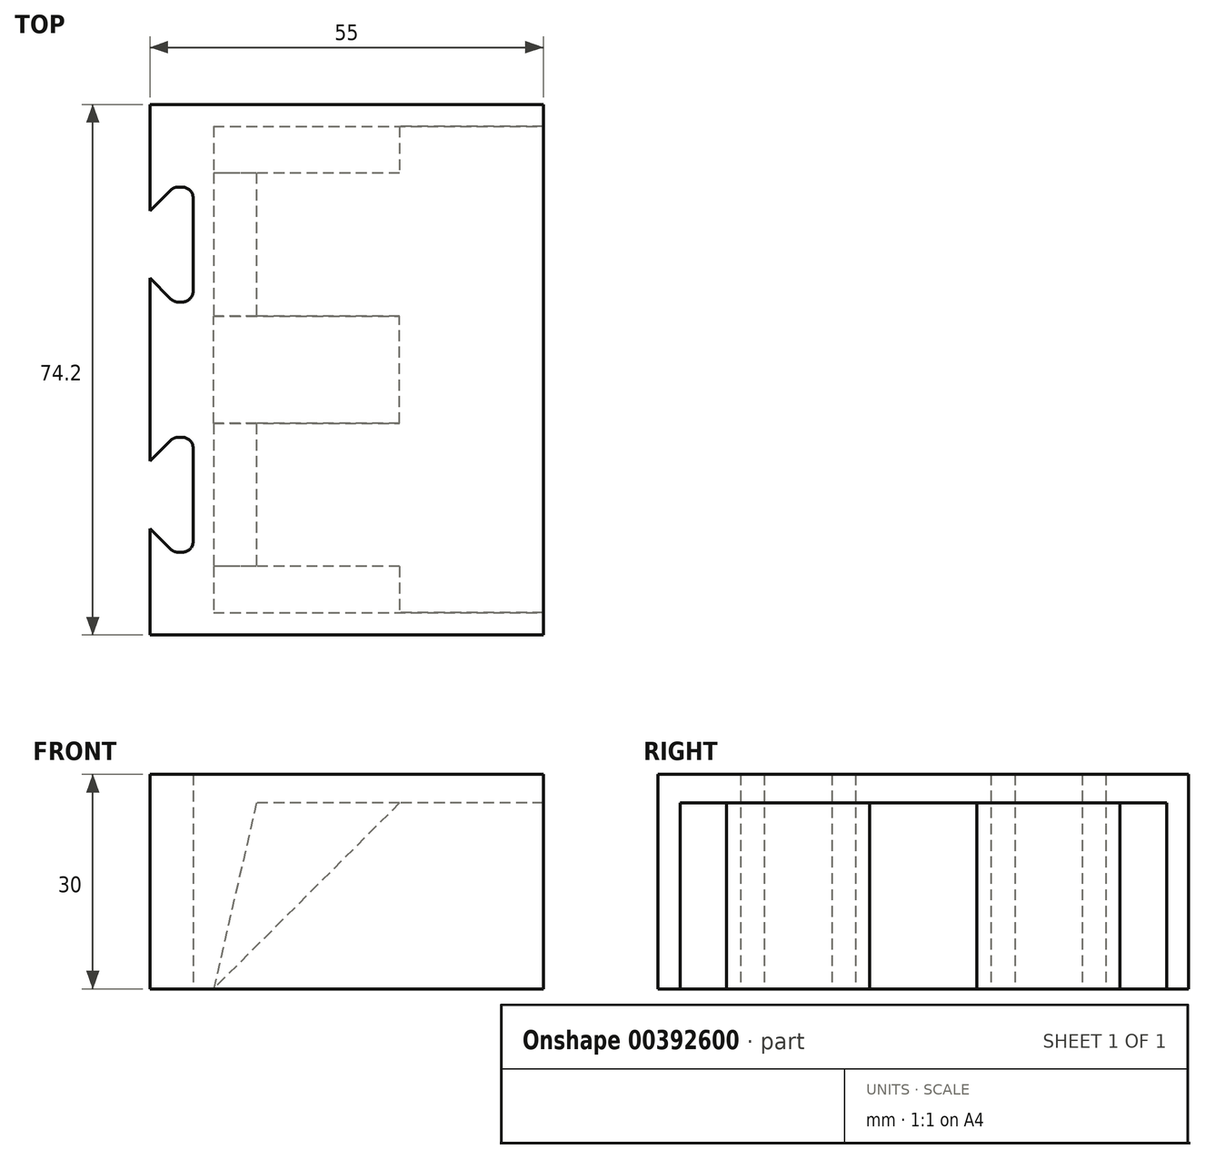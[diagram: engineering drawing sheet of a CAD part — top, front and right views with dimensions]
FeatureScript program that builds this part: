
annotation { "Feature Type Name" : "Feature", "Feature Type Description" : "" }
export const myFeature = defineFeature(function(context is Context, id is Id, definition is map)
    precondition{}
    {
        {
            var Q0;
            Q0=qCreatedBy(makeId("Top.planeOp"),FACE);
            var sketch = newSketch(context, id + "F0", { "sketchPlane" : qUnion([Q0])});
            skLineSegment(sketch, "E0.bottom", {"start": v(90, -35) * mm, "end": v(0, -35) * mm});
            skLineSegment(sketch, "E0.top", {"start": v(90, 35) * mm, "end": v(0, 35) * mm});
            skLineSegment(sketch, "E0.left", {"start": v(90, -35) * mm, "end": v(90, 35) * mm});
            skPoint(sketch, "E0.middle", {"position": v(0, 0) * mm});
            skPoint(sketch, "E1.middle", {"position": v(49.8, 0) * mm});
            skLineSegment(sketch, "E2", {"start": v(0, 0) * mm, "end": v(24, 0) * mm, "construction": true});
            skLineSegment(sketch, "E3", {"start": v(0, 0) * mm, "end": v(0, -14) * mm, "construction": true});
            skLineSegment(sketch, "E4", {"start": v(0, 0) * mm, "end": v(-35, 0) * mm, "construction": true});
            skLineSegment(sketch, "E5.bottom", {"start": v(-5, -19.5) * mm, "end": v(5, -19.5) * mm});
            skLineSegment(sketch, "E5.top", {"start": v(-5, 19.5) * mm, "end": v(5, 19.5) * mm});
            skLineSegment(sketch, "E5.left", {"start": v(-5, -19.5) * mm, "end": v(-5, 19.5) * mm});
            skLineSegment(sketch, "E5.right", {"start": v(5, -19.5) * mm, "end": v(5, 19.5) * mm});
            skLineSegment(sketch, "E6.bottom", {"start": v(-40, -17.25) * mm, "end": v(-30, -17.25) * mm});
            skLineSegment(sketch, "E6.top", {"start": v(-40, 17.25) * mm, "end": v(-30, 17.25) * mm});
            skLineSegment(sketch, "E6.left", {"start": v(-40, -17.25) * mm, "end": v(-40, 17.25) * mm});
            skLineSegment(sketch, "E6.right", {"start": v(-30, -17.25) * mm, "end": v(-30, 17.25) * mm});
            skPoint(sketch, "E6.middle", {"position": v(-35, 0) * mm});
            skLineSegment(sketch, "E7", {"start": v(0, 35) * mm, "end": v(0, 23) * mm});
            skPoint(sketch, "E7.endSnap0", {"position": v(0, 35) * mm});
            skLineSegment(sketch, "E8", {"start": v(0, 23) * mm, "end": v(-50, 23) * mm});
            skLineSegment(sketch, "E9", {"start": v(-50, 23) * mm, "end": v(-50, 0) * mm});
            skLineSegment(sketch, "E10.MirrorCS", {"start": v(-50, -23) * mm, "end": v(-50, 0) * mm});
            skLineSegment(sketch, "E11.MirrorCS", {"start": v(0, -35) * mm, "end": v(0, -23) * mm});
            skLineSegment(sketch, "E12.MirrorCS", {"start": v(0, -23) * mm, "end": v(-50, -23) * mm});
            skPoint(sketch, "E0.right.end.orphan", {"position": v(-90, 35) * mm});
            skPoint(sketch, "E13.orphan", {"position": v(-90, -35) * mm});
            skLineSegment(sketch, "E14.0", {"start": v(92.1, -37.1) * mm, "end": v(92.1, 37.1) * mm});
            skLineSegment(sketch, "E14.1", {"start": v(92.1, -37.1) * mm, "end": v(-2.1, -37.1) * mm});
            skLineSegment(sketch, "E14.2", {"start": v(92.1, 37.1) * mm, "end": v(-2.1, 37.1) * mm});
            skLineSegment(sketch, "E14.3", {"start": v(-2.1, -37.1) * mm, "end": v(-2.1, -25.1) * mm});
            skLineSegment(sketch, "E14.4", {"start": v(-2.1, -25.1) * mm, "end": v(-52.1, -25.1) * mm});
            skLineSegment(sketch, "E14.5", {"start": v(-2.1, 37.1) * mm, "end": v(-2.1, 25.1) * mm});
            skLineSegment(sketch, "E14.6", {"start": v(-2.1, 25.1) * mm, "end": v(-52.1, 25.1) * mm});
            skLineSegment(sketch, "E14.7", {"start": v(-52.1, 25.1) * mm, "end": v(-52.1, 0) * mm});
            skLineSegment(sketch, "E14.8", {"start": v(-52.1, -25.1) * mm, "end": v(-52.1, 0) * mm});
            skLineSegment(sketch, "E15.bottom", {"start": v(-30, 52.75) * mm, "end": v(-40, 52.75) * mm});
            skLineSegment(sketch, "E15.top", {"start": v(-30, 87.25) * mm, "end": v(-40, 87.25) * mm});
            skLineSegment(sketch, "E15.left", {"start": v(-30, 52.75) * mm, "end": v(-30, 87.25) * mm});
            skLineSegment(sketch, "E15.right", {"start": v(-40, 52.75) * mm, "end": v(-40, 87.25) * mm});
            skPoint(sketch, "E15.middle", {"position": v(-35, 70) * mm});
            skLineSegment(sketch, "E16.bottom", {"start": v(-5, 50.5) * mm, "end": v(5, 50.5) * mm});
            skLineSegment(sketch, "E16.top", {"start": v(-5, 89.5) * mm, "end": v(5, 89.5) * mm});
            skLineSegment(sketch, "E16.left", {"start": v(-5, 50.5) * mm, "end": v(-5, 89.5) * mm});
            skLineSegment(sketch, "E16.right", {"start": v(5, 50.5) * mm, "end": v(5, 89.5) * mm});
            skPoint(sketch, "E16.middle", {"position": v(0, 70) * mm});
            skPoint(sketch, "E16.middle.positionSnap0", {"position": v(-30, 70) * mm});
            skPoint(sketch, "E16.centerSnap0", {"position": v(-30, 70) * mm});
            skLineSegment(sketch, "E17", {"start": v(-35, 0) * mm, "end": v(-35, 70) * mm, "construction": true});
            skCircle(sketch, "E18", {"center": v(0, -14) * mm, "radius": 2 * mm});
            skLineSegment(sketch, "E19", {"start": v(-35, 0) * mm, "end": v(-35, -11.75) * mm, "construction": true});
            skCircle(sketch, "E20", {"center": v(-35, -11.75) * mm, "radius": 2 * mm});
            skCircle(sketch, "E21.MirrorC", {"center": v(-35, 11.75) * mm, "radius": 2 * mm});
            skCircle(sketch, "E22.MirrorC", {"center": v(0, 14) * mm, "radius": 2 * mm});
            skLineSegment(sketch, "E23", {"start": v(-35, 70) * mm, "end": v(-35, 81.75) * mm, "construction": true});
            skLineSegment(sketch, "E24", {"start": v(0, 70) * mm, "end": v(0, 84) * mm, "construction": true});
            skCircle(sketch, "E25", {"center": v(-35, 81.75) * mm, "radius": 2 * mm});
            skCircle(sketch, "E26", {"center": v(0, 84) * mm, "radius": 2 * mm});
            skLineSegment(sketch, "E27", {"start": v(-35, 70) * mm, "end": v(-30, 70) * mm, "construction": true});
            skCircle(sketch, "E28.MirrorC", {"center": v(-35, 58.25) * mm, "radius": 2 * mm});
            skCircle(sketch, "E29.MirrorC", {"center": v(0, 56) * mm, "radius": 2 * mm});
            skLineSegment(sketch, "E30", {"start": v(90, -35) * mm, "end": v(92.1, -35) * mm});
            skLineSegment(sketch, "E31", {"start": v(90, 35) * mm, "end": v(92.1, 35) * mm});
            skLineSegment(sketch, "E32", {"start": v(-2.1, 37.1) * mm, "end": v(-6.1, 37.1) * mm});
            skLineSegment(sketch, "E33", {"start": v(-6.1, 37.1) * mm, "end": v(-6.1, 25.1) * mm});
            skLineSegment(sketch, "E34", {"start": v(-2.1, -37.1) * mm, "end": v(-6.1, -37.1) * mm});
            skLineSegment(sketch, "E35", {"start": v(-6.1, -37.1) * mm, "end": v(-6.1, -25.1) * mm});
            skLineSegment(sketch, "E36", {"start": v(-41, 23) * mm, "end": v(-41, 11) * mm});
            skLineSegment(sketch, "E37", {"start": v(-41, 11) * mm, "end": v(-50, 11) * mm});
            skPoint(sketch, "E38.end.orphan", {"position": v(-41, 14.45) * mm});
            skLineSegment(sketch, "E39.MirrorCS", {"start": v(-41, -11) * mm, "end": v(-50, -11) * mm});
            skLineSegment(sketch, "E40.MirrorCS", {"start": v(-41, -23) * mm, "end": v(-41, -11) * mm});
            skLineSegment(sketch, "E41", {"start": v(90, -35) * mm, "end": v(90, -37.1) * mm});
            skLineSegment(sketch, "E42", {"start": v(90, 35) * mm, "end": v(90, 37.1) * mm});
            skLineSegment(sketch, "E43.bottom", {"start": v(90, 35) * mm, "end": v(86, 35) * mm});
            skLineSegment(sketch, "E43.left", {"start": v(90, 35) * mm, "end": v(90, 23) * mm});
            skLineSegment(sketch, "E44.bottom", {"start": v(90, -35) * mm, "end": v(86, -35) * mm});
            skLineSegment(sketch, "E44.left", {"start": v(90, -35) * mm, "end": v(90, -23) * mm});
            skLineSegment(sketch, "E45.bottom", {"start": v(86, -35) * mm, "end": v(80, -35) * mm});
            skLineSegment(sketch, "E46.bottom", {"start": v(86, 35) * mm, "end": v(80, 35) * mm});
            skLineSegment(sketch, "E47.bottom", {"start": v(0, 23) * mm, "end": v(7, 23) * mm});
            skLineSegment(sketch, "E47.top", {"start": v(0, 35) * mm, "end": v(12, 35) * mm});
            skLineSegment(sketch, "E47.left", {"start": v(0, 23) * mm, "end": v(0, 35) * mm});
            skLineSegment(sketch, "E47.right", {"start": v(12, 28) * mm, "end": v(12, 35) * mm});
            skLineSegment(sketch, "E48.bottom", {"start": v(0, -35) * mm, "end": v(12, -35) * mm});
            skLineSegment(sketch, "E48.top", {"start": v(0, -23) * mm, "end": v(7, -23) * mm});
            skLineSegment(sketch, "E48.right", {"start": v(12, -35) * mm, "end": v(12, -28) * mm});
            skCircle(sketch, "E49", {"center": v(6, -29) * mm, "radius": 2 * mm});
            skPoint(sketch, "E49.centerSnap0", {"position": v(6, -35) * mm});
            skPoint(sketch, "E49.centerSnap1", {"position": v(0, -29) * mm});
            skPoint(sketch, "E50.visualSharp", {"position": v(12, -23) * mm});
            skArc(sketch, "E50.filletArc", {"start": v(12, -28) * mm, "mid": v(10.54, -24.46) * mm, "end": v(7, -23) * mm});
            skPoint(sketch, "E51.visualSharp", {"position": v(12, 23) * mm});
            skArc(sketch, "E51.filletArc", {"start": v(7, 23) * mm, "mid": v(10.54, 24.46) * mm, "end": v(12, 28) * mm});
            skCircle(sketch, "E52.MirrorC", {"center": v(6, 29) * mm, "radius": 2 * mm});
            skCircle(sketch, "E53", {"center": v(6, 29) * mm, "radius": 4.5 * mm});
            skCircle(sketch, "E54.MirrorC", {"center": v(6, -29) * mm, "radius": 4.5 * mm});
            skCircle(sketch, "E55", {"center": v(0, 14) * mm, "radius": 6 * mm});
            skCircle(sketch, "E56", {"center": v(-35, 11.75) * mm, "radius": 6 * mm});
            skCircle(sketch, "E57", {"center": v(-35, -11.75) * mm, "radius": 6 * mm});
            skCircle(sketch, "E58", {"center": v(0, -14) * mm, "radius": 6 * mm});
            skLineSegment(sketch, "E59", {"start": v(-6.1, 25.1) * mm, "end": v(-6.08, 23) * mm});
            skLineSegment(sketch, "E60", {"start": v(-6.1, -25.1) * mm, "end": v(-6.1, -23) * mm});
            skLineSegment(sketch, "E61", {"start": v(-47.66, 23) * mm, "end": v(-47.66, 18) * mm, "construction": true});
            skLineSegment(sketch, "E62", {"start": v(-50, 18) * mm, "end": v(-45, 18) * mm, "construction": true});
            skCircle(sketch, "E63", {"center": v(-45, 18) * mm, "radius": 2.25 * mm});
            skCircle(sketch, "E64.MirrorC", {"center": v(-45, -18) * mm, "radius": 2.25 * mm});
            skCircle(sketch, "E65.MirrorC", {"center": v(-25, 18) * mm, "radius": 2.25 * mm});
            skCircle(sketch, "E66.MirrorC", {"center": v(-25, -18) * mm, "radius": 2.25 * mm});
            skCircle(sketch, "E67.MirrorC", {"center": v(28.54, -17.75) * mm, "radius": 2.25 * mm});
            skLineSegment(sketch, "E68.bottom", {"start": v(34.04, -22.75) * mm, "end": v(23.04, -22.75) * mm});
            skLineSegment(sketch, "E68.top", {"start": v(34.04, -12.75) * mm, "end": v(23.04, -12.75) * mm});
            skLineSegment(sketch, "E68.left", {"start": v(36.04, -20.75) * mm, "end": v(36.04, -14.75) * mm});
            skLineSegment(sketch, "E68.right", {"start": v(21.04, -20.75) * mm, "end": v(21.04, -14.75) * mm});
            skLineSegment(sketch, "E69.0", {"start": v(36.44, -12.35) * mm, "end": v(20.64, -12.35) * mm});
            skLineSegment(sketch, "E69.1", {"start": v(36.44, -23.15) * mm, "end": v(36.44, -12.35) * mm});
            skLineSegment(sketch, "E69.2", {"start": v(36.44, -23.15) * mm, "end": v(20.64, -23.15) * mm});
            skLineSegment(sketch, "E69.3", {"start": v(20.64, -23.15) * mm, "end": v(20.64, -12.35) * mm});
            skPoint(sketch, "E70.visualSharp", {"position": v(21.04, -12.75) * mm});
            skArc(sketch, "E70.filletArc", {"start": v(23.04, -12.75) * mm, "mid": v(21.62, -13.33) * mm, "end": v(21.04, -14.75) * mm});
            skPoint(sketch, "E71.visualSharp", {"position": v(36.04, -12.75) * mm});
            skArc(sketch, "E71.filletArc", {"start": v(36.04, -14.75) * mm, "mid": v(35.45, -13.33) * mm, "end": v(34.04, -12.75) * mm});
            skPoint(sketch, "E72.visualSharp", {"position": v(36.04, -22.75) * mm});
            skArc(sketch, "E72.filletArc", {"start": v(34.04, -22.75) * mm, "mid": v(35.45, -22.16) * mm, "end": v(36.04, -20.75) * mm});
            skPoint(sketch, "E73.visualSharp", {"position": v(21.04, -22.75) * mm});
            skArc(sketch, "E73.filletArc", {"start": v(21.04, -20.75) * mm, "mid": v(21.62, -22.16) * mm, "end": v(23.04, -22.75) * mm});
            skArc(sketch, "E74.0", {"start": v(39.54, -14.75) * mm, "mid": v(37.93, -10.86) * mm, "end": v(34.04, -9.25) * mm});
            skLineSegment(sketch, "E74.1", {"start": v(39.54, -20.75) * mm, "end": v(39.54, -14.75) * mm});
            skLineSegment(sketch, "E74.2", {"start": v(34.04, -9.25) * mm, "end": v(23.04, -9.25) * mm});
            skArc(sketch, "E74.3", {"start": v(34.04, -26.25) * mm, "mid": v(37.93, -24.64) * mm, "end": v(39.54, -20.75) * mm});
            skArc(sketch, "E74.4", {"start": v(23.04, -9.25) * mm, "mid": v(19.15, -10.86) * mm, "end": v(17.54, -14.75) * mm});
            skLineSegment(sketch, "E74.5", {"start": v(17.54, -20.75) * mm, "end": v(17.54, -14.75) * mm});
            skArc(sketch, "E74.6", {"start": v(17.54, -20.75) * mm, "mid": v(19.15, -24.64) * mm, "end": v(23.04, -26.25) * mm});
            skLineSegment(sketch, "E74.7", {"start": v(34.04, -26.25) * mm, "end": v(23.04, -26.25) * mm});
            skLineSegment(sketch, "E75", {"start": v(45, 37.1) * mm, "end": v(45, -37.1) * mm});
            skLineSegment(sketch, "E76", {"start": v(45, 31.57) * mm, "end": v(68, 31.57) * mm, "construction": true});
            skLineSegment(sketch, "E77", {"start": v(68, 35) * mm, "end": v(68, -35) * mm});
            skLineSegment(sketch, "E78", {"start": v(12, -28) * mm, "end": v(12, 28) * mm});
            skLineSegment(sketch, "E79", {"start": v(12, 35) * mm, "end": v(12, 37.1) * mm});
            skLineSegment(sketch, "E80", {"start": v(68, 35) * mm, "end": v(68, 37.1) * mm});
            skLineSegment(sketch, "E81", {"start": v(68, 31.57) * mm, "end": v(70.1, 31.57) * mm, "construction": true});
            skLineSegment(sketch, "E82", {"start": v(70.1, 37.1) * mm, "end": v(70.1, -37.1) * mm});
            skLineSegment(sketch, "E83", {"start": v(12, -35) * mm, "end": v(12, -37.1) * mm});
            skLineSegment(sketch, "E84", {"start": v(72.96, 0) * mm, "end": v(72.96, 17.5) * mm, "construction": true});
            skPoint(sketch, "E84.startSnap0", {"position": v(70.1, 0) * mm});
            skLineSegment(sketch, "E85", {"start": v(70.1, 13.5) * mm, "end": v(73.34, 10.26) * mm});
            skPoint(sketch, "E86.end.orphan", {"position": v(71.21, 13.5) * mm});
            skPoint(sketch, "E86.start.orphan", {"position": v(71.21, 17.5) * mm});
            skLineSegment(sketch, "E87", {"start": v(74.05, 9.96) * mm, "end": v(74.64, 9.96) * mm});
            skLineSegment(sketch, "E88", {"start": v(72.96, 17.5) * mm, "end": v(71.21, 17.5) * mm, "construction": true});
            skLineSegment(sketch, "E89.MirrorCS", {"start": v(70.1, 21.5) * mm, "end": v(73.34, 24.74) * mm});
            skLineSegment(sketch, "E90.MirrorCS", {"start": v(74.05, 25.04) * mm, "end": v(74.64, 25.04) * mm});
            skLineSegment(sketch, "E91", {"start": v(75.64, 24.04) * mm, "end": v(75.64, 10.96) * mm});
            skPoint(sketch, "E92.visualSharp", {"position": v(75.64, 25.04) * mm});
            skArc(sketch, "E92.filletArc", {"start": v(75.64, 24.04) * mm, "mid": v(75.34, 24.74) * mm, "end": v(74.64, 25.04) * mm});
            skPoint(sketch, "E93.visualSharp", {"position": v(73.64, 25.04) * mm});
            skArc(sketch, "E93.filletArc", {"start": v(74.05, 25.04) * mm, "mid": v(73.67, 24.96) * mm, "end": v(73.34, 24.74) * mm});
            skPoint(sketch, "E94.visualSharp", {"position": v(73.64, 9.96) * mm});
            skArc(sketch, "E94.filletArc", {"start": v(73.34, 10.26) * mm, "mid": v(73.67, 10.04) * mm, "end": v(74.05, 9.96) * mm});
            skPoint(sketch, "E95.visualSharp", {"position": v(75.64, 9.96) * mm});
            skArc(sketch, "E95.filletArc", {"start": v(74.64, 9.96) * mm, "mid": v(75.34, 10.26) * mm, "end": v(75.64, 10.96) * mm});
            skLineSegment(sketch, "E96.MirrorCS", {"start": v(70.1, -13.5) * mm, "end": v(73.34, -10.26) * mm});
            skArc(sketch, "E97.MirrorCS", {"start": v(73.34, -10.26) * mm, "mid": v(73.67, -10.04) * mm, "end": v(74.05, -9.96) * mm});
            skLineSegment(sketch, "E98.MirrorCS", {"start": v(74.05, -9.96) * mm, "end": v(74.64, -9.96) * mm});
            skArc(sketch, "E99.MirrorCS", {"start": v(74.64, -9.96) * mm, "mid": v(75.34, -10.26) * mm, "end": v(75.64, -10.96) * mm});
            skLineSegment(sketch, "E100.MirrorCS", {"start": v(75.64, -24.04) * mm, "end": v(75.64, -10.96) * mm});
            skLineSegment(sketch, "E101.MirrorCS", {"start": v(70.1, -21.5) * mm, "end": v(73.34, -24.74) * mm});
            skArc(sketch, "E102.MirrorCS", {"start": v(74.05, -25.04) * mm, "mid": v(73.67, -24.96) * mm, "end": v(73.34, -24.74) * mm});
            skLineSegment(sketch, "E103.MirrorCS", {"start": v(74.05, -25.04) * mm, "end": v(74.64, -25.04) * mm});
            skArc(sketch, "E104.MirrorCS", {"start": v(75.64, -24.04) * mm, "mid": v(75.34, -24.74) * mm, "end": v(74.64, -25.04) * mm});
            skLineSegment(sketch, "E105", {"start": v(68, -35) * mm, "end": v(56.64, -23.64) * mm, "construction": true});
            skArc(sketch, "E106.MirrorCS", {"start": v(43.26, -40.34) * mm, "mid": v(43.04, -40.67) * mm, "end": v(42.96, -41.05) * mm});
            skArc(sketch, "E107.MirrorCS", {"start": v(58.04, -41.05) * mm, "mid": v(57.96, -40.67) * mm, "end": v(57.74, -40.34) * mm});
            skArc(sketch, "E108.MirrorCS", {"start": v(42.96, -41.64) * mm, "mid": v(43.26, -42.34) * mm, "end": v(43.96, -42.64) * mm});
            skArc(sketch, "E109.MirrorCS", {"start": v(57.04, -42.64) * mm, "mid": v(57.74, -42.34) * mm, "end": v(58.04, -41.64) * mm});
            skLineSegment(sketch, "E110.MirrorCS", {"start": v(42.96, -41.05) * mm, "end": v(42.96, -41.64) * mm});
            skLineSegment(sketch, "E111.MirrorCS", {"start": v(58.04, -41.05) * mm, "end": v(58.04, -41.64) * mm});
            skLineSegment(sketch, "E112.MirrorCS", {"start": v(57.04, -42.64) * mm, "end": v(43.96, -42.64) * mm});
            skLineSegment(sketch, "E113.MirrorCS", {"start": v(46.5, -37.1) * mm, "end": v(43.26, -40.34) * mm});
            skLineSegment(sketch, "E114.MirrorCS", {"start": v(54.5, -37.1) * mm, "end": v(57.74, -40.34) * mm});
            skLineSegment(sketch, "E115", {"start": v(36.04, -37.1) * mm, "end": v(36.04, -40.15) * mm, "construction": true});
            skLineSegment(sketch, "E116.MirrorCS", {"start": v(14.04, -41.05) * mm, "end": v(14.04, -41.64) * mm});
            skArc(sketch, "E117.MirrorCS", {"start": v(14.04, -41.05) * mm, "mid": v(14.12, -40.67) * mm, "end": v(14.33, -40.34) * mm});
            skLineSegment(sketch, "E118.MirrorCS", {"start": v(29.11, -41.05) * mm, "end": v(29.11, -41.64) * mm});
            skArc(sketch, "E119.MirrorCS", {"start": v(28.82, -40.34) * mm, "mid": v(29.04, -40.67) * mm, "end": v(29.11, -41.05) * mm});
            skArc(sketch, "E120.MirrorCS", {"start": v(15.04, -42.64) * mm, "mid": v(14.33, -42.34) * mm, "end": v(14.04, -41.64) * mm});
            skLineSegment(sketch, "E121.MirrorCS", {"start": v(15.04, -42.64) * mm, "end": v(28.11, -42.64) * mm});
            skArc(sketch, "E122.MirrorCS", {"start": v(29.11, -41.64) * mm, "mid": v(28.82, -42.34) * mm, "end": v(28.11, -42.64) * mm});
            skLineSegment(sketch, "E123.MirrorCS", {"start": v(17.58, -37.1) * mm, "end": v(14.33, -40.34) * mm});
            skLineSegment(sketch, "E124.MirrorCS", {"start": v(25.58, -37.1) * mm, "end": v(28.82, -40.34) * mm});
            skLineSegment(sketch, "E125", {"start": v(28.54, -17.75) * mm, "end": v(28.54, 0) * mm, "construction": true});
            skLineSegment(sketch, "E126", {"start": v(28.54, 0) * mm, "end": v(56.04, 0) * mm, "construction": true});
            skLineSegment(sketch, "E127.bottom", {"start": v(53.54, 20) * mm, "end": v(58.54, 20) * mm});
            skLineSegment(sketch, "E127.top", {"start": v(53.54, -20) * mm, "end": v(58.54, -20) * mm});
            skLineSegment(sketch, "E127.left", {"start": v(53.54, 20) * mm, "end": v(53.54, -20) * mm});
            skLineSegment(sketch, "E127.right", {"start": v(58.54, 20) * mm, "end": v(58.54, -20) * mm});
            skPoint(sketch, "E127.middle", {"position": v(56.04, 0) * mm});
            skLineSegment(sketch, "E128", {"start": v(28.54, -17.75) * mm, "end": v(28.54, -35) * mm, "construction": true});
            skPoint(sketch, "E128.endSnap0", {"position": v(28.54, -26.25) * mm});
            skLineSegment(sketch, "E129", {"start": v(28.54, -17.75) * mm, "end": v(12, -17.75) * mm, "construction": true});
            skLineSegment(sketch, "E130", {"start": v(12, 17.54) * mm, "end": v(28.54, 17.54) * mm, "construction": true});
            skLineSegment(sketch, "E131", {"start": v(28.54, 17.54) * mm, "end": v(28.54, 35) * mm, "construction": true});
            skArc(sketch, "E132.MirrorCS", {"start": v(36.04, 14.75) * mm, "mid": v(35.45, 13.33) * mm, "end": v(34.04, 12.75) * mm});
            skArc(sketch, "E133.MirrorCS", {"start": v(23.04, 12.75) * mm, "mid": v(21.62, 13.33) * mm, "end": v(21.04, 14.75) * mm});
            skArc(sketch, "E134.MirrorCS", {"start": v(21.04, 20.75) * mm, "mid": v(21.62, 22.16) * mm, "end": v(23.04, 22.75) * mm});
            skArc(sketch, "E135.MirrorCS", {"start": v(34.04, 22.75) * mm, "mid": v(35.45, 22.16) * mm, "end": v(36.04, 20.75) * mm});
            skArc(sketch, "E136.MirrorCS", {"start": v(23.04, 9.25) * mm, "mid": v(19.15, 10.86) * mm, "end": v(17.54, 14.75) * mm});
            skLineSegment(sketch, "E137.MirrorCS", {"start": v(34.04, 9.25) * mm, "end": v(23.04, 9.25) * mm});
            skPoint(sketch, "E138.MirrorP", {"position": v(36.04, 12.75) * mm});
            skArc(sketch, "E139.MirrorCS", {"start": v(34.04, 26.25) * mm, "mid": v(37.93, 24.64) * mm, "end": v(39.54, 20.75) * mm});
            skArc(sketch, "E140.MirrorCS", {"start": v(17.54, 20.75) * mm, "mid": v(19.15, 24.64) * mm, "end": v(23.04, 26.25) * mm});
            skPoint(sketch, "E141.MirrorP", {"position": v(28.54, 17.75) * mm});
            skLineSegment(sketch, "E142.MirrorCS", {"start": v(36.44, 23.15) * mm, "end": v(20.64, 23.15) * mm});
            skPoint(sketch, "E143.MirrorP", {"position": v(21.04, 12.75) * mm});
            skLineSegment(sketch, "E144.MirrorCS", {"start": v(34.04, 26.25) * mm, "end": v(23.04, 26.25) * mm});
            skPoint(sketch, "E145.MirrorP", {"position": v(21.04, 22.75) * mm});
            skLineSegment(sketch, "E146.MirrorCS", {"start": v(20.64, 23.15) * mm, "end": v(20.64, 12.35) * mm});
            skLineSegment(sketch, "E147.MirrorCS", {"start": v(36.44, 12.35) * mm, "end": v(20.64, 12.35) * mm});
            skLineSegment(sketch, "E148.MirrorCS", {"start": v(17.54, 20.75) * mm, "end": v(17.54, 14.75) * mm});
            skCircle(sketch, "E149.MirrorC", {"center": v(28.54, 17.75) * mm, "radius": 2.25 * mm});
            skPoint(sketch, "E150.MirrorP", {"position": v(28.54, 26.25) * mm});
            skPoint(sketch, "E151.MirrorP", {"position": v(36.04, 22.75) * mm});
            skLineSegment(sketch, "E152.MirrorCS", {"start": v(21.04, 20.75) * mm, "end": v(21.04, 14.75) * mm});
            skLineSegment(sketch, "E153.MirrorCS", {"start": v(39.54, 20.75) * mm, "end": v(39.54, 14.75) * mm});
            skLineSegment(sketch, "E154.MirrorCS", {"start": v(36.44, 23.15) * mm, "end": v(36.44, 12.35) * mm});
            skLineSegment(sketch, "E155.MirrorCS", {"start": v(34.04, 22.75) * mm, "end": v(23.04, 22.75) * mm});
            skArc(sketch, "E156.MirrorCS", {"start": v(39.54, 14.75) * mm, "mid": v(37.93, 10.86) * mm, "end": v(34.04, 9.25) * mm});
            skLineSegment(sketch, "E157.MirrorCS", {"start": v(34.04, 12.75) * mm, "end": v(23.04, 12.75) * mm});
            skLineSegment(sketch, "E158.MirrorCS", {"start": v(36.04, 20.75) * mm, "end": v(36.04, 14.75) * mm});
            skArc(sketch, "E159.MirrorCS", {"start": v(29.11, 41.64) * mm, "mid": v(28.82, 42.34) * mm, "end": v(28.11, 42.64) * mm});
            skArc(sketch, "E160.MirrorCS", {"start": v(28.82, 40.34) * mm, "mid": v(29.04, 40.67) * mm, "end": v(29.11, 41.05) * mm});
            skArc(sketch, "E161.MirrorCS", {"start": v(15.04, 42.64) * mm, "mid": v(14.33, 42.34) * mm, "end": v(14.04, 41.64) * mm});
            skArc(sketch, "E162.MirrorCS", {"start": v(14.04, 41.05) * mm, "mid": v(14.12, 40.67) * mm, "end": v(14.33, 40.34) * mm});
            skArc(sketch, "E163.MirrorCS", {"start": v(57.04, 42.64) * mm, "mid": v(57.74, 42.34) * mm, "end": v(58.04, 41.64) * mm});
            skArc(sketch, "E164.MirrorCS", {"start": v(58.04, 41.05) * mm, "mid": v(57.96, 40.67) * mm, "end": v(57.74, 40.34) * mm});
            skLineSegment(sketch, "E165.MirrorCS", {"start": v(42.96, 41.05) * mm, "end": v(42.96, 41.64) * mm});
            skLineSegment(sketch, "E166.MirrorCS", {"start": v(58.04, 41.05) * mm, "end": v(58.04, 41.64) * mm});
            skLineSegment(sketch, "E167.MirrorCS", {"start": v(14.04, 41.05) * mm, "end": v(14.04, 41.64) * mm});
            skLineSegment(sketch, "E168.MirrorCS", {"start": v(29.11, 41.05) * mm, "end": v(29.11, 41.64) * mm});
            skArc(sketch, "E169.MirrorCS", {"start": v(42.96, 41.64) * mm, "mid": v(43.26, 42.34) * mm, "end": v(43.96, 42.64) * mm});
            skArc(sketch, "E170.MirrorCS", {"start": v(43.26, 40.34) * mm, "mid": v(43.04, 40.67) * mm, "end": v(42.96, 41.05) * mm});
            skLineSegment(sketch, "E171.MirrorCS", {"start": v(57.04, 42.64) * mm, "end": v(43.96, 42.64) * mm});
            skLineSegment(sketch, "E172.MirrorCS", {"start": v(15.04, 42.64) * mm, "end": v(28.11, 42.64) * mm});
            skLineSegment(sketch, "E173.MirrorCS", {"start": v(17.58, 37.1) * mm, "end": v(14.33, 40.34) * mm});
            skLineSegment(sketch, "E174.MirrorCS", {"start": v(25.58, 37.1) * mm, "end": v(28.82, 40.34) * mm});
            skLineSegment(sketch, "E175.MirrorCS", {"start": v(46.5, 37.1) * mm, "end": v(43.26, 40.34) * mm});
            skLineSegment(sketch, "E176.MirrorCS", {"start": v(54.5, 37.1) * mm, "end": v(57.74, 40.34) * mm});
            skLineSegment(sketch, "E177", {"start": v(92.1, 37.1) * mm, "end": v(125.1, 37.1) * mm});
            skLineSegment(sketch, "E178", {"start": v(125.1, 37.1) * mm, "end": v(125.1, -37.1) * mm});
            skLineSegment(sketch, "E179", {"start": v(125.1, -37.1) * mm, "end": v(92.1, -37.1) * mm});
            skLineSegment(sketch, "E180", {"start": v(125.1, 30.14) * mm, "end": v(123, 30.14) * mm, "construction": true});
            skLineSegment(sketch, "E181.0", {"start": v(70.1, 12.8) * mm, "end": v(72.99, 9.9) * mm});
            skArc(sketch, "E181.1", {"start": v(72.99, 9.9) * mm, "mid": v(73.48, 9.58) * mm, "end": v(74.05, 9.46) * mm});
            skLineSegment(sketch, "E181.2", {"start": v(74.05, 9.46) * mm, "end": v(74.64, 9.46) * mm});
            skArc(sketch, "E181.3", {"start": v(74.64, 9.46) * mm, "mid": v(75.7, 9.9) * mm, "end": v(76.14, 10.96) * mm});
            skLineSegment(sketch, "E181.4", {"start": v(76.14, 24.04) * mm, "end": v(76.14, 10.96) * mm});
            skLineSegment(sketch, "E181.5", {"start": v(70.1, 22.2) * mm, "end": v(72.99, 25.1) * mm});
            skArc(sketch, "E181.6", {"start": v(74.05, 25.54) * mm, "mid": v(73.48, 25.42) * mm, "end": v(72.99, 25.1) * mm});
            skLineSegment(sketch, "E181.7", {"start": v(74.05, 25.54) * mm, "end": v(74.64, 25.54) * mm});
            skArc(sketch, "E181.8", {"start": v(76.14, 24.04) * mm, "mid": v(75.7, 25.1) * mm, "end": v(74.64, 25.54) * mm});
            skLineSegment(sketch, "E182.MirrorCS", {"start": v(70.1, -12.8) * mm, "end": v(72.99, -9.9) * mm});
            skArc(sketch, "E183.MirrorCS", {"start": v(72.99, -9.9) * mm, "mid": v(73.48, -9.58) * mm, "end": v(74.05, -9.46) * mm});
            skLineSegment(sketch, "E184.MirrorCS", {"start": v(74.05, -9.46) * mm, "end": v(74.64, -9.46) * mm});
            skArc(sketch, "E185.MirrorCS", {"start": v(74.64, -9.46) * mm, "mid": v(75.7, -9.9) * mm, "end": v(76.14, -10.96) * mm});
            skLineSegment(sketch, "E186.MirrorCS", {"start": v(76.14, -24.04) * mm, "end": v(76.14, -10.96) * mm});
            skArc(sketch, "E187.MirrorCS", {"start": v(76.14, -24.04) * mm, "mid": v(75.7, -25.1) * mm, "end": v(74.64, -25.54) * mm});
            skLineSegment(sketch, "E188.MirrorCS", {"start": v(74.05, -25.54) * mm, "end": v(74.64, -25.54) * mm});
            skArc(sketch, "E189.MirrorCS", {"start": v(74.05, -25.54) * mm, "mid": v(73.48, -25.42) * mm, "end": v(72.99, -25.1) * mm});
            skLineSegment(sketch, "E190.MirrorCS", {"start": v(70.1, -22.2) * mm, "end": v(72.99, -25.1) * mm});
            skLineSegment(sketch, "E191.0", {"start": v(45.8, -37.1) * mm, "end": v(42.9, -39.99) * mm});
            skArc(sketch, "E191.1", {"start": v(42.9, -39.99) * mm, "mid": v(42.58, -40.48) * mm, "end": v(42.46, -41.05) * mm});
            skLineSegment(sketch, "E191.2", {"start": v(42.46, -41.05) * mm, "end": v(42.46, -41.64) * mm});
            skArc(sketch, "E191.3", {"start": v(42.46, -41.64) * mm, "mid": v(42.9, -42.7) * mm, "end": v(43.96, -43.14) * mm});
            skLineSegment(sketch, "E191.4", {"start": v(57.04, -43.14) * mm, "end": v(43.96, -43.14) * mm});
            skLineSegment(sketch, "E191.5", {"start": v(55.2, -37.1) * mm, "end": v(58.1, -39.99) * mm});
            skArc(sketch, "E191.6", {"start": v(58.54, -41.05) * mm, "mid": v(58.42, -40.48) * mm, "end": v(58.1, -39.99) * mm});
            skLineSegment(sketch, "E191.7", {"start": v(58.54, -41.05) * mm, "end": v(58.54, -41.64) * mm});
            skArc(sketch, "E191.8", {"start": v(57.04, -43.14) * mm, "mid": v(58.1, -42.7) * mm, "end": v(58.54, -41.64) * mm});
            skLineSegment(sketch, "E192.MirrorCS", {"start": v(26.28, -37.1) * mm, "end": v(29.17, -39.99) * mm});
            skArc(sketch, "E193.MirrorCS", {"start": v(29.17, -39.99) * mm, "mid": v(29.5, -40.48) * mm, "end": v(29.61, -41.05) * mm});
            skLineSegment(sketch, "E194.MirrorCS", {"start": v(29.61, -41.05) * mm, "end": v(29.61, -41.64) * mm});
            skArc(sketch, "E195.MirrorCS", {"start": v(29.61, -41.64) * mm, "mid": v(29.17, -42.7) * mm, "end": v(28.11, -43.14) * mm});
            skLineSegment(sketch, "E196.MirrorCS", {"start": v(15.04, -43.14) * mm, "end": v(28.11, -43.14) * mm});
            skArc(sketch, "E197.MirrorCS", {"start": v(15.04, -43.14) * mm, "mid": v(13.98, -42.7) * mm, "end": v(13.54, -41.64) * mm});
            skLineSegment(sketch, "E198.MirrorCS", {"start": v(13.54, -41.05) * mm, "end": v(13.54, -41.64) * mm});
            skArc(sketch, "E199.MirrorCS", {"start": v(13.54, -41.05) * mm, "mid": v(13.66, -40.48) * mm, "end": v(13.98, -39.99) * mm});
            skLineSegment(sketch, "E200.MirrorCS", {"start": v(16.87, -37.1) * mm, "end": v(13.98, -39.99) * mm});
            skSolve(sketch);
        }
        {
            var Q0;
            Q0=makeQuery(id+"F0.imprint","IMPRINT",FACE,{"disambiguationData":[TD([[makeQuery(id+"F0.imprint","IMPRINT",EDGE,{"derivedFrom":sQuery(id+"F0.wireOp",EDGE,"E0.left")}),1.0]])]});
            var Q1;
            {var subQ0=sQuery(id+"F0.wireOp",EDGE,"E42");Q1=makeQuery(id+"F0.imprint","IMPRINT",FACE,{"disambiguationData":[TD([[makeQuery(id+"F0.imprint","IMPRINT",EDGE,{"derivedFrom":subQ0}),1.0]])]});}
            var Q2;
            Q2=makeQuery(id+"F0.imprint","IMPRINT",FACE,{"disambiguationData":[TD([[makeQuery(id+"F0.imprint","IMPRINT",EDGE,{"derivedFrom":sQuery(id+"F0.wireOp",EDGE,"E0.left")}),-1.0]])]});
            var Q3;
            {var subQ3=sQuery(id+"F0.wireOp",EDGE,"E31");Q3=makeQuery(id+"F0.imprint","IMPRINT",FACE,{"disambiguationData":[TD([[makeQuery(id+"F0.imprint","IMPRINT",EDGE,{"derivedFrom":subQ3}),1.0]])]});}
            var Q4;
            {var subQ0=sQuery(id+"F0.wireOp",EDGE,"E177");Q4=makeQuery(id+"F0.imprint","IMPRINT",FACE,{"disambiguationData":[TD([[makeQuery(id+"F0.imprint","IMPRINT",EDGE,{"derivedFrom":subQ0}),-1.0]])]});}
            var Q5;
            {var subQ5=sQuery(id+"F0.wireOp",EDGE,"E41");Q5=makeQuery(id+"F0.imprint","IMPRINT",FACE,{"disambiguationData":[TD([[makeQuery(id+"F0.imprint","IMPRINT",EDGE,{"derivedFrom":subQ5}),-1.0]])]});}
            var Q6;
            {var subQ3=sQuery(id+"F0.wireOp",EDGE,"E30");Q6=makeQuery(id+"F0.imprint","IMPRINT",FACE,{"disambiguationData":[TD([[makeQuery(id+"F0.imprint","IMPRINT",EDGE,{"derivedFrom":subQ3}),-1.0]])]});}
            extrude(context, id + "F1", {"entities" : qUnion([Q0, Q1, Q2, Q3, Q4, Q5, Q6]), "depth" : 30 * mm});
        }
        {
            var Q0;
            Q0=qCreatedBy(makeId("Top.planeOp"),FACE);
            cPlane(context, id + "F2", {"entities" : qUnion([Q0]), "cplaneType" : CPlaneType.OFFSET, "offset" : 10 * mm, "width" : 150 * mm, "height" : 150 * mm});
        }
        {
            var Q0;
            Q0=qCreatedBy(makeId("Front.planeOp"),FACE);
            var sketch = newSketch(context, id + "F3", { "sketchPlane" : qUnion([Q0])});
            skLineSegment(sketch, "E201", {"start": v(0, 0) * mm, "end": v(79, 0) * mm, "construction": true});
            skLineSegment(sketch, "E202", {"start": v(79, 0) * mm, "end": v(125.1, 0) * mm});
            skLineSegment(sketch, "E203", {"start": v(125.1, 0) * mm, "end": v(125.1, 26) * mm});
            skLineSegment(sketch, "E204", {"start": v(79, 0) * mm, "end": v(105, 26) * mm});
            skLineSegment(sketch, "E205", {"start": v(125.1, 26) * mm, "end": v(105, 26) * mm});
            skLineSegment(sketch, "E206", {"start": v(105, 26) * mm, "end": v(85, 26) * mm});
            skLineSegment(sketch, "E207", {"start": v(85, 26) * mm, "end": v(79, 0) * mm});
            skSolve(sketch);
        }
        {
            var Q0;
            Q0=makeQuery(id+"F3.imprint","IMPRINT",FACE,{"disambiguationData":[TD([[makeQuery(id+"F3.imprint","IMPRINT",EDGE,{"derivedFrom":sQuery(id+"F3.wireOp",EDGE,"E202")}),1.0]])]});
            extrude(context, id + "F4", {"entities" : qUnion([Q0]), "operationType" : NewBodyOperationType.REMOVE, "endBound" : BoundingType.SYMMETRIC, "oppositeDirection" : true, "depth" : 68 * mm});
        }
        {
            var Q0;
            Q0 = qSketchRegion(id + "F3", true);
            extrude(context, id + "F5", {"entities" : qUnion([Q0]), "operationType" : NewBodyOperationType.REMOVE, "endBound" : BoundingType.SYMMETRIC, "oppositeDirection" : true, "depth" : 55 * mm});
        }
        {
            var Q0;
            Q0=makeQuery(id+"F3.imprint","IMPRINT",FACE,{"disambiguationData":[TD([[makeQuery(id+"F3.imprint","IMPRINT",EDGE,{"derivedFrom":sQuery(id+"F3.wireOp",EDGE,"E204")}),1.0]])]});
            extrude(context, id + "F6", {"entities" : qUnion([Q0]), "operationType" : NewBodyOperationType.ADD, "endBound" : BoundingType.SYMMETRIC, "depth" : 15 * mm});
        }
    });
